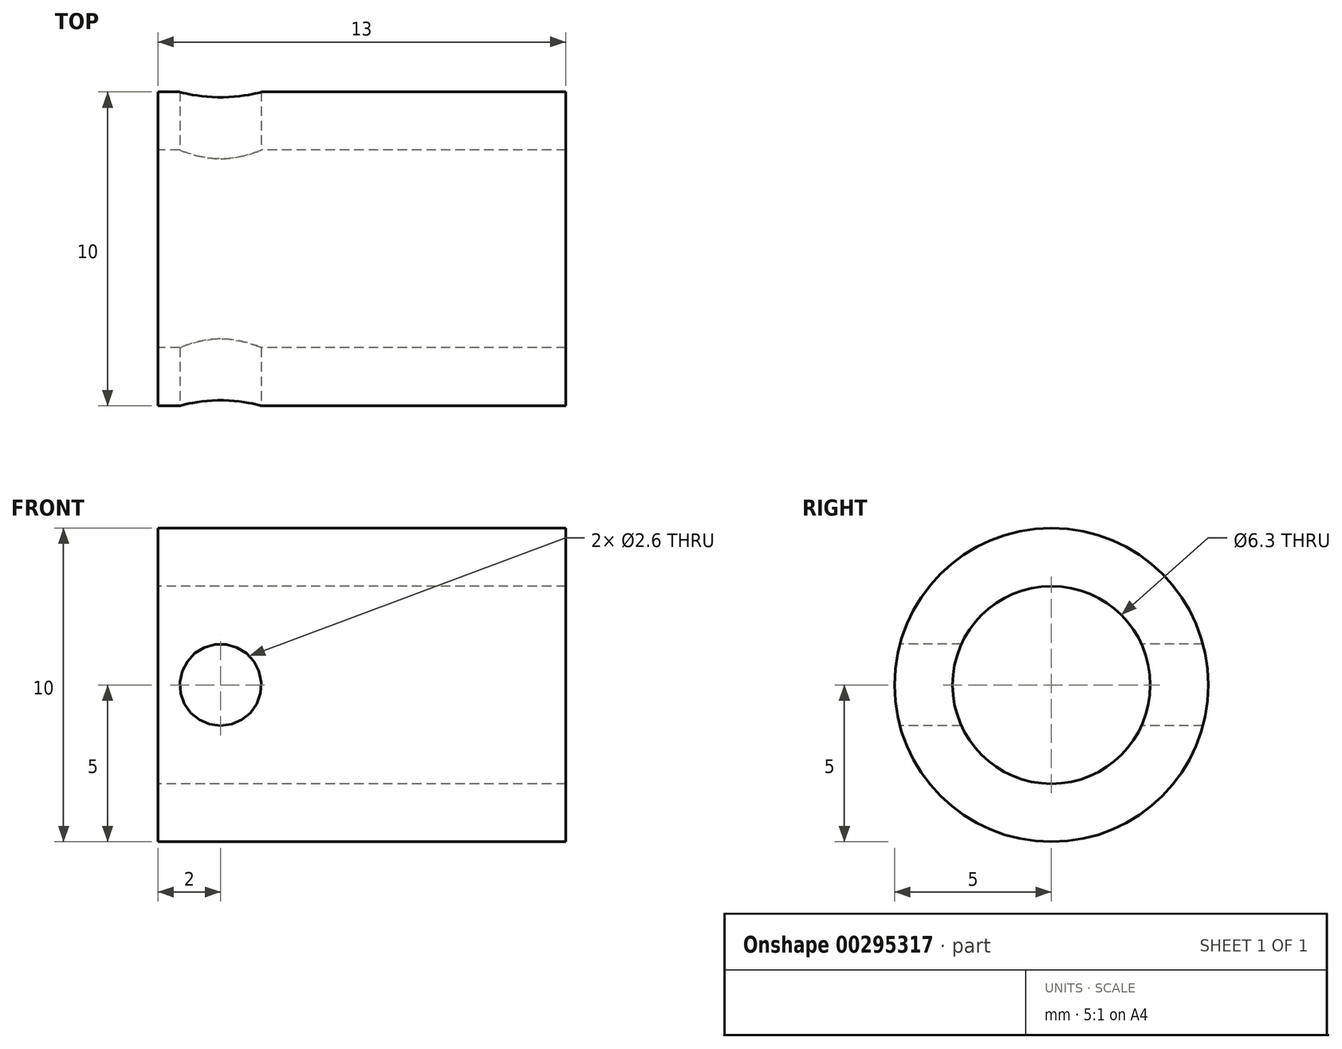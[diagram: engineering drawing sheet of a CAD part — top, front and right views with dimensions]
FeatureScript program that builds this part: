
annotation { "Feature Type Name" : "Feature", "Feature Type Description" : "" }
export const myFeature = defineFeature(function(context is Context, id is Id, definition is map)
    precondition{}
    {
        {
            var Q0;
            Q0=qCreatedBy(makeId("Right.planeOp"),FACE);
            var sketch = newSketch(context, id + "F0", { "sketchPlane" : qUnion([Q0])});
            skCircle(sketch, "E0", {"center": v(0, 0) * mm, "radius": 3.15 * mm});
            skCircle(sketch, "E1", {"center": v(0, 0) * mm, "radius": 5 * mm});
            skSolve(sketch);
        }
        {
            var Q0;
            Q0=makeQuery(id+"F0.imprint","IMPRINT",FACE,{"disambiguationData":[TD([[makeQuery(id+"F0.imprint","IMPRINT",EDGE,{"derivedFrom":sQuery(id+"F0.wireOp",EDGE,"E0")}),-1.0]])]});
            extrude(context, id + "F1", {"entities" : qUnion([Q0]), "depth" : 13 * mm});
        }
        {
            var Q0;
            Q0=qCreatedBy(makeId("Front.planeOp"),FACE);
            var sketch = newSketch(context, id + "F2", { "sketchPlane" : qUnion([Q0])});
            skCircle(sketch, "E2", {"center": v(0, 0) * mm, "radius": 2 * mm, "construction": true});
            skCircle(sketch, "E3", {"center": v(2, 0) * mm, "radius": 1.3 * mm});
            skSolve(sketch);
        }
        {
            var Q0;
            Q0=makeQuery(id+"F2.imprint","IMPRINT",FACE,{"disambiguationData":[TD([[makeQuery(id+"F2.imprint","IMPRINT",EDGE,{"derivedFrom":sQuery(id+"F2.wireOp",EDGE,"E3")}),1.0]])]});
            extrude(context, id + "F3", {"entities" : qUnion([Q0]), "operationType" : NewBodyOperationType.REMOVE, "endBound" : BoundingType.THROUGH_ALL, "oppositeDirection" : true, "depth" : 25 * mm, "hasSecondDirection" : true, "secondDirectionBound" : SecondDirectionBoundingType.THROUGH_ALL, "secondDirectionOppositeDirection" : false, "secondDirectionDepth" : 25 * mm});
        }
    });
